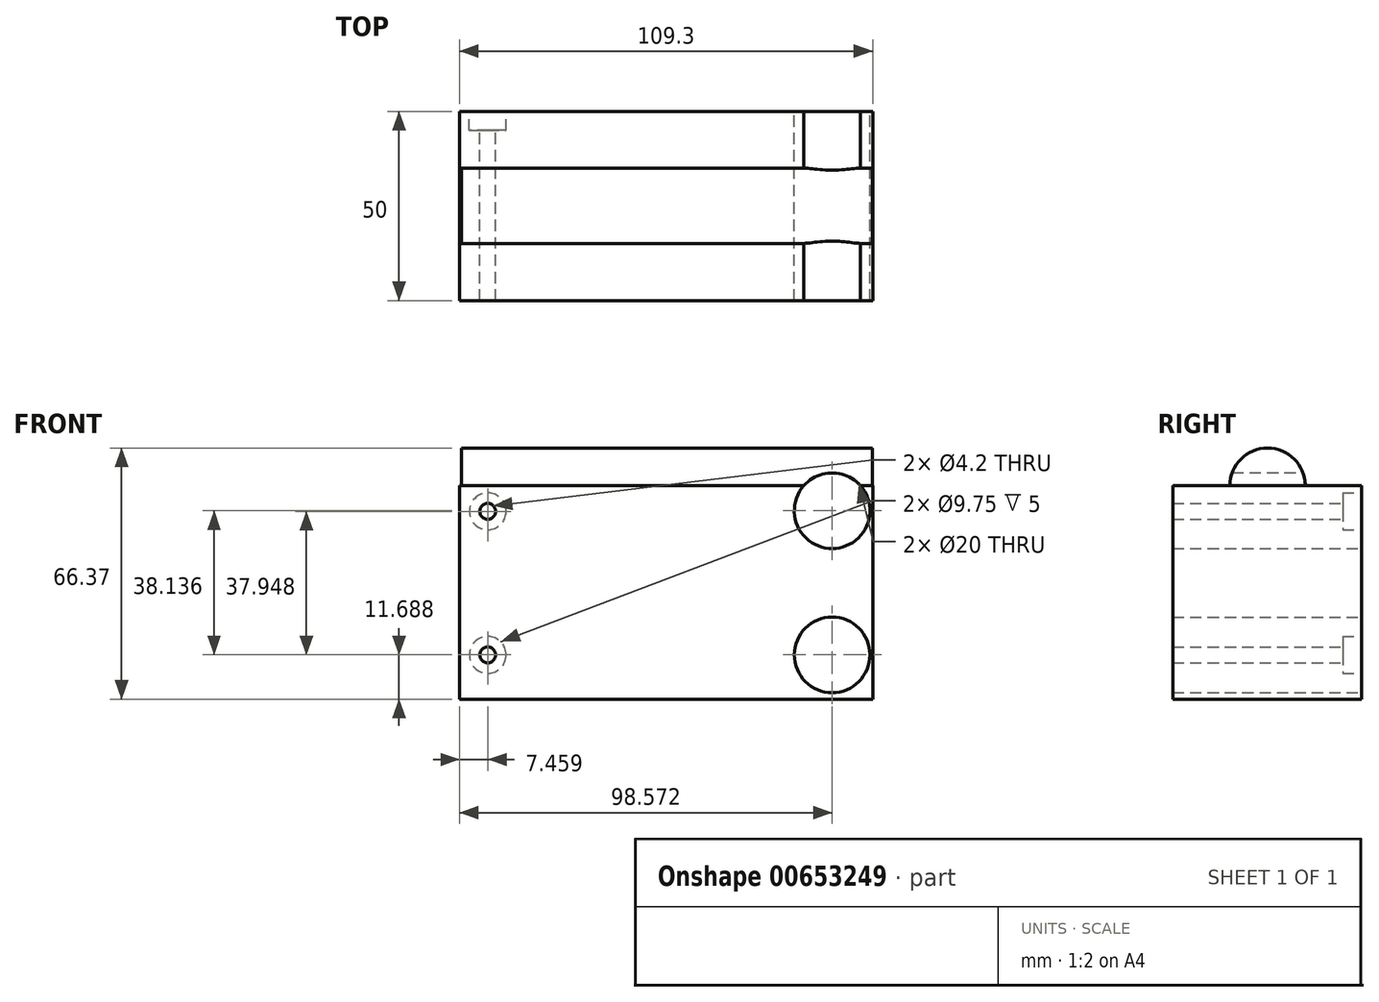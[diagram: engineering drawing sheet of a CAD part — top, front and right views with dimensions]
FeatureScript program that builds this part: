
annotation { "Feature Type Name" : "Feature", "Feature Type Description" : "" }
export const myFeature = defineFeature(function(context is Context, id is Id, definition is map)
    precondition{}
    {
        {
            var Q0;
            Q0=qCreatedBy(makeId("Front.planeOp"),FACE);
            var sketch = newSketch(context, id + "F0", { "sketchPlane" : qUnion([Q0])});
            skLineSegment(sketch, "E0.bottom", {"start": v(54.65, 28.23) * mm, "end": v(-54.65, 28.23) * mm});
            skLineSegment(sketch, "E0.top", {"start": v(54.65, -28.23) * mm, "end": v(-54.65, -28.23) * mm});
            skLineSegment(sketch, "E0.left", {"start": v(54.65, 28.23) * mm, "end": v(54.65, -28.23) * mm});
            skLineSegment(sketch, "E0.right", {"start": v(-54.65, 28.23) * mm, "end": v(-54.65, -28.23) * mm});
            skPoint(sketch, "E0.middle", {"position": v(0, 0) * mm});
            skSolve(sketch);
        }
        {
            var Q0;
            Q0 = qSketchRegion(id + "F0", true);
            extrude(context, id + "F1", {"entities" : qUnion([Q0]), "depth" : 50 * mm, "offsetDistance" : 25 * mm});
        }
        {
            var Q0;
            Q0=makeQuery(id+"F1.opExtrude","CAP_FACE",FACE,{"disambiguationData":[OSD([sQuery(id+"F0.wireOp",EDGE,"E0.bottom"),sQuery(id+"F0.wireOp",EDGE,"E0.top"),sQuery(id+"F0.wireOp",EDGE,"E0.left"),sQuery(id+"F0.wireOp",EDGE,"E0.right")])],"isStart":true});
            var sketch = newSketch(context, id + "F2", { "sketchPlane" : qUnion([Q0])});
            skCircle(sketch, "E1", {"center": v(0, 21.96) * mm, "radius": 21.76 * mm});
            skSolve(sketch);
        }
        {
            var Q0;
            Q0=sQuery(id+"F2.wireOp",EDGE,"E1");
            extrude(context, id + "F3", {"bodyType" : ToolBodyType.SURFACE, "operationType" : NewBodyOperationType.REMOVE, "surfaceEntities" : qUnion([Q0]), "oppositeDirection" : true, "depth" : 50 * mm, "offsetDistance" : 25 * mm});
        }
        {
            var Q0;
            Q0=qCreatedBy(makeId("Right.planeOp"),FACE);
            var sketch = newSketch(context, id + "F4", { "sketchPlane" : qUnion([Q0])});
            skCircle(sketch, "E2", {"center": v(-24.9, 28.17) * mm, "radius": 9.97 * mm});
            skSolve(sketch);
        }
        {
            var Q0;
            Q0 = qSketchRegion(id + "F4", true);
            extrude(context, id + "F5", {"entities" : qUnion([Q0]), "operationType" : NewBodyOperationType.ADD, "depth" : 54.6 * mm, "offsetDistance" : 25 * mm});
        }
        {
            var Q0;
            Q0 = qSketchRegion(id + "F4", true);
            extrude(context, id + "F6", {"entities" : qUnion([Q0]), "operationType" : NewBodyOperationType.ADD, "oppositeDirection" : true, "depth" : 54.2 * mm, "offsetDistance" : 25 * mm});
        }
        {
            var Q0;
            Q0=qCreatedBy(makeId("Front.planeOp"),FACE);
            var sketch = newSketch(context, id + "F7", { "sketchPlane" : qUnion([Q0])});
            skLineSegment(sketch, "E3", {"start": v(-47.2, 21.4) * mm, "end": v(-47.2, -16.54) * mm});
            skSolve(sketch);
        }
        {
            var Q0;
            Q0=sQuery(id+"F7.wireOp",VERTEX,"E3.start");
            var Q1;
            Q1=sQuery(id+"F7.wireOp",VERTEX,"E3.end");
            var Q2;
            Q2=makeQuery(id+"F1.opExtrude","SWEPT_BODY",BODY,{"disambiguationData":[OSD([sQuery(id+"F0.wireOp",EDGE,"E0.bottom"),sQuery(id+"F0.wireOp",EDGE,"E0.top"),sQuery(id+"F0.wireOp",EDGE,"E0.left"),sQuery(id+"F0.wireOp",EDGE,"E0.right")])]});
            hole(context, id + "F8", {"style" : HoleStyle.C_BORE, "endStyle" : HoleEndStyle.THROUGH, "oppositeDirection" : true, "standardTappedOrClearance" : lookupTablePath({ "standard" : "ISO", "engagement" : "75%", "pitch" : "0.8 mm", "size" : "M5", "type" : "Tapped" }), "standardBlindInLast" : lookupTablePath({ "standard" : "ISO", "engagement" : "75%", "pitch" : "0.8 mm", "size" : "M5", "type" : "Tapped" }), "holeDiameter" : 4.2 * mm, "cBoreDiameter" : 9.75 * mm, "cBoreDepth" : 5 * mm, "majorDiameter" : 5 * mm, "showTappedDepth" : true, "isTappedThrough" : true, "tappedDepth" : 12 * mm, "tapClearance" : 3, "locations" : qUnion([Q0, Q1]), "scope" : qUnion([Q2])});
        }
        {
            var Q0;
            Q0=qCreatedBy(makeId("Front.planeOp"),FACE);
            var sketch = newSketch(context, id + "F9", { "sketchPlane" : qUnion([Q0])});
            skLineSegment(sketch, "E4", {"start": v(117.38, 13.9) * mm, "end": v(132.78, 13.9) * mm});
            skLineSegment(sketch, "E5", {"start": v(132.78, 13.9) * mm, "end": v(117.38, 13.9) * mm});
            skLineSegment(sketch, "E6", {"start": v(-47.2, 21.6) * mm, "end": v(43.92, 21.6) * mm});
            skLineSegment(sketch, "E7", {"start": v(-47.2, -16.54) * mm, "end": v(42.98, -16.54) * mm});
            skLineSegment(sketch, "E8", {"start": v(43.92, 21.6) * mm, "end": v(43.92, -16.54) * mm});
            skSolve(sketch);
        }
        {
            var Q0;
            Q0=sQuery(id+"F9.wireOp",VERTEX,"E6.end");
            var Q1;
            Q1=sQuery(id+"F9.wireOp",VERTEX,"E8.end");
            var Q2;
            Q2=makeQuery(id+"F1.opExtrude","SWEPT_BODY",BODY,{"disambiguationData":[OSD([sQuery(id+"F0.wireOp",EDGE,"E0.bottom"),sQuery(id+"F0.wireOp",EDGE,"E0.top"),sQuery(id+"F0.wireOp",EDGE,"E0.left"),sQuery(id+"F0.wireOp",EDGE,"E0.right")])]});
            hole(context, id + "F10", {"style" : HoleStyle.C_BORE, "endStyle" : HoleEndStyle.THROUGH, "oppositeDirection" : true, "holeDiameter" : 20 * mm, "cBoreDiameter" : 20 * mm, "cBoreDepth" : 20 * mm, "majorDiameter" : 5 * mm, "isTappedThrough" : true, "tappedDepth" : 12 * mm, "tapClearance" : 3, "locations" : qUnion([Q0, Q1]), "scope" : qUnion([Q2])});
        }
    });
